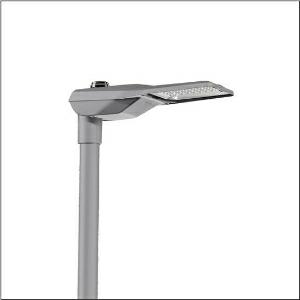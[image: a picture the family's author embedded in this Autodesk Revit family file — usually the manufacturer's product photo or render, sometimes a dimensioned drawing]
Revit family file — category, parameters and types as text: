
# Revit family: streetlight_sl_21_mini___st0_5a_5xe6b47n08gb_d394
name_source: partatom
category: Lighting Fixtures
units: mm (PartAtom-declared; Revit-internal decimal feet)

## family parameters
Cut with Voids When Loaded = No
Host = Face
Light Source = No
Part Type = Normal
Room Calculation Point = No
Round Connector Dimension = Use Diameter
Shared = No

## types (1)
- --- (1 x LED, 6180 lm, 40.4 W, 4000K)
    Apparent Load = 40 VA
    CIE Flux Codes = 41 75 97 100 100
    Color Rendering = 70
    Color Temperature = 4000K
    Default Elevation = 1800 mm
    Description = Streetlight SL 21 mini, mast luminaire, primary light control with lens, of PMMA, primary optical cover: cover, of toughened safety glass, transparent, light distribution: ST0.5a, light emission: direct distribution, primary light characteristic: asymmetric, installation type: side-entry, LED, 3G 1.5mm², High Power LED, rated luminous flux: 6.180lm, luminous efficacy: 153lm/W, light colour: 740, colour temperature: 4000K, control gear: NEMA (7pin), control: overheat protection, pre-setting: linear dimming characteristic, constant luminous flux control, time-dependent luminous flux control, flexible luminous flux parameterisation, mains connection: 230..240V, AC, 50/60Hz, connection cable pre-assembled, cable length: 8,5m, wiring characteristics: H07RN-F, start of lifetime: 40W, end of service life: 41W, reduction: 19W, luminaire housing, of diecast aluminium (EN AC-44300), powder-coated, Siteco® metallic grey (DB 702S), corrosivity category C5 mid according to DIN EN ISO 12944, multi-level sealing system, sealing non-destructively replaceable, inclination adjustable: 0°, 5°, 10°, 15°, length: 628mm, width: 235mm, height: 110mm, spigot size: 42mm (side-entry), mounting height: 4..8m, protection rating (complete): IP66, insulation class (complete): insulation class I (protective earthing), certification: CE, ENEC, ENEC+, VDE, impact resistance: IK10, permissible operating ambient temperature for outdoor applications: -40..+50°C, standard-compliant lighting for roads and squares, packaging unit: 1 piece

Light Distribution: ST0.5a
    Height = 110 mm
    Lamp = 1 x LED
    Lamp Light Flux = 6180 lm
    Lamp Power = 40.4 W
    Lamp count = 1
    Length = 625 mm
    Luminous efficacy = 153 lm/W
    Manufacturer = Siteco
    ModVariant = No
    Model = 5XE6B47N08GB
    Number of Poles = 1
    OnlyDefault = Yes
    Power Factor = 1
    Product Name = Streetlight SL 21 mini | ST0.5a
    Product group = mast luminaire | pylon top
    ProductGroupID = 6100
    Protection Class = Protection class I
    Protection Degree = IP 66
    RLX_Detail_Level = 1
    RLX_Emergency_Light_Flux = 0 lm
    RLX_Emergency_Type = 0
    RLX_Emergency_Type_DB = No
    RlxData = <blob elided: 36813 chars, md5=7ea3ee89>
    Socket = socket
    Standby Power = 0 W
    System Light Flux = 6180 lm
    System Power = 40 W
    Type Comments = factory setting: luminous flux: 100 % | dim-lin: 254 | 812 mA
    Type Image = l_1294379.jpg
    URL = http://relux.com
    VarID = @adj_158937
    Voltage = 0 V
    Weight = 0.00 kg
    Width = 234 mm

## geometry (parser evidence)
native form markers: Blend x4, Sweep x11
no freeform markers — native parametric forms only
